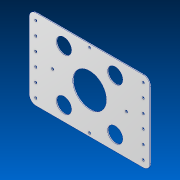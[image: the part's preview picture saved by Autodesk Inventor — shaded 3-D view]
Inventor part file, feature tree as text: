
AUTODESK INVENTOR PART (.ipt)
format: ipt  version: 2022.2 (Build 262287000, 287)  size: 157,184 bytes
history: native  units: in
note: dims shown in document units (in); Inventor stores cm internally (conversion verified against a paired STEP export)
features: sketch x1, extrude x1, hole x1
ambient origin geometry x8: Origin, YZ Plane, XZ Plane, XY Plane, X Axis, Y Axis, Z Axis, Center Point
bodies: Solid1 (feature_tree)
feature tree (3):
  sketch  "Sketch1"  dims[d1=2.7in d2=1.125in d3=2.5in d4=9.0in d5=0.5in d6=0.5in d7=1.0in d8=1.0in d10=1.0in d11=1.0in d12=1.0in d13=1.0in d14=0.5in d15=0.5in d16=0.5in d17=0.25in d18=2.7in d19=0.064in d20=0.0in d21=2.0in d22=0.17in d23=0.75in d24=0.375in d25=0.25in d26=0.5635in d27=1.0in d28=0.8108in]
  extrude  "Extrusion1"  Depth=0.064in
  hole  "Hole1"  [1 undecoded]
note: 1 required parameter value undecoded (feature->parameter linkage not recoverable at this tier; creation-order binding heuristic only, values carry confidence <= 0.55)
